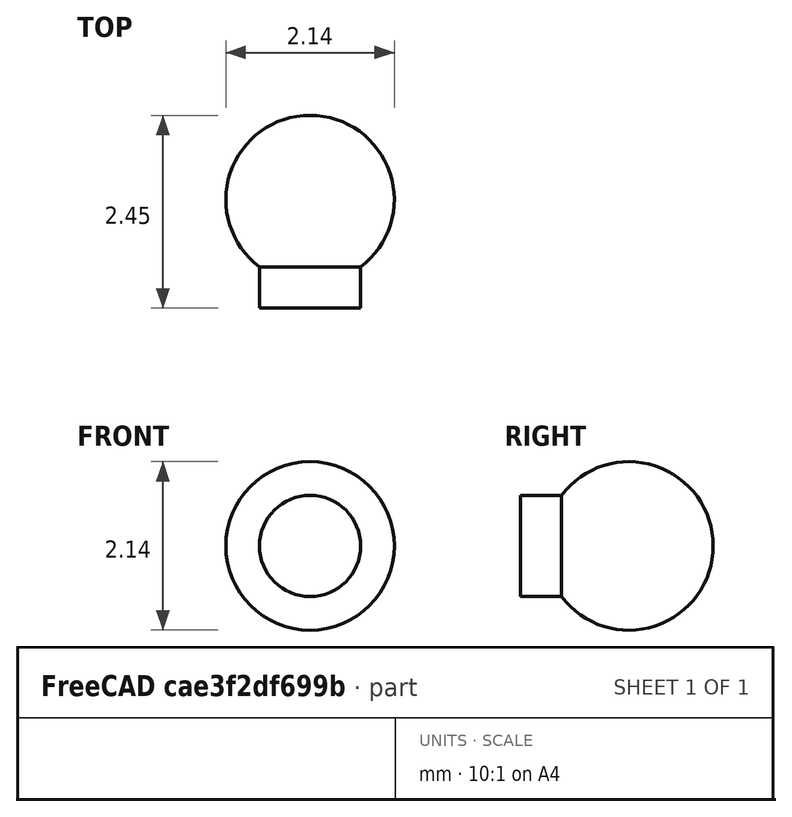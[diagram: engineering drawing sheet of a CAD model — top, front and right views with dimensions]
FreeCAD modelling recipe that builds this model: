
FCSTD DOCUMENT  (FreeCAD 1.1R20260325 (Git shallow))
Label: Lampada_personalizada
License: All rights reserved
LicenseURL: https://en.wikipedia.org/wiki/All_rights_reserved
objects: App::DocumentObjectGroup×5, App::Point×1, Sketcher::SketchObject×1, PartDesign::Revolution×1, PartDesign::Body×1
note: 6 computed .brp shape members not serialized (recipe doc carries the construction recipe); baked Part::Feature solids carry a one-line shape summary decoded from their .brp

FEATURE [App::DocumentObjectGroup] Simbolo_2D
FEATURE [App::DocumentObjectGroup] Foto
FEATURE [App::DocumentObjectGroup] Modelo_3D
FEATURE [App::DocumentObjectGroup] Descricao
FEATURE [App::DocumentObjectGroup] Detalhes_2D
FEATURE [App::Point] Origin001
  Role = Origin
FEATURE [Sketcher::SketchObject] Sketch
  ArcFitTolerance = 1e-06
  AttachmentSupport = -> [Origin]
  ExternalTypes = [0]
  FullyConstrained = false
  MakeInternals = false
  MapMode = 5
  _ExternalGeoVersion = 1
  sketch-geometry (4):
    g0: ArcOfCircle CenterX=0 CenterY=3.46988 CenterZ=0 NormalX=0 NormalY=0 NormalZ=1 AngleXU=0 Radius=1.07016 StartAngle=5.35661 EndAngle=7.85398
    g1: LineSegment StartX=0.64271 StartY=2.6142 StartZ=0 EndX=0.64271 EndY=2.09395 EndZ=0
    g2: LineSegment StartX=0.64271 StartY=2.09395 StartZ=0 EndX=0 EndY=2.09395 EndZ=0
    g3: LineSegment StartX=3e-16 StartY=4.54004 StartZ=0 EndX=0 EndY=2.09395 EndZ=0
  constraints (9):
    c: PointOnObject(g0,g-2)
    c: PointOnObject(g0,g-2)
    c: Coincident(g1,g0)
    c: Vertical(g1)
    c: Coincident(g2,g1)
    c: PointOnObject(g2,g-2)
    c: Horizontal(g2)
    c: Coincident(g3,g0)
    c: Coincident(g3,g2)
FEATURE [PartDesign::Revolution] Revolution
  Angle = 360
  Angle2 = 0
  Axis = (0,1,0)
  Base = (0,0,0)
  FuseOrder = 0
  Profile = -> Sketch
  ReferenceAxis = -> Sketch [V_Axis]
  Refine = true
  Reversed = true
  Suppressed = false
  Type = 0
FEATURE [PartDesign::Body] Body
  AllowCompound = false
  Group = -> [Sketch,Revolution]
  Origin = -> Origin
  Tip = -> Revolution
